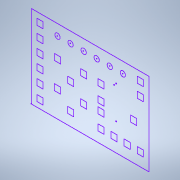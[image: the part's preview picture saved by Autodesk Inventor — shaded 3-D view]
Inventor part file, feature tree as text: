
AUTODESK INVENTOR PART (.ipt)
format: ipt  version: 2021.1 (Build 251245000, 245)  size: 135,168 bytes
history: native  units: mm
features: sketch x1
ambient origin geometry x8: Origin, YZ Plane, XZ Plane, XY Plane, X Axis, Y Axis, Z Axis, Center Point
feature tree (1):
  sketch  "Sketch2"
